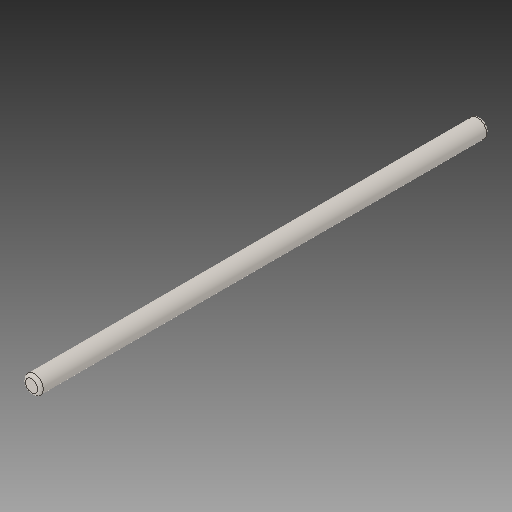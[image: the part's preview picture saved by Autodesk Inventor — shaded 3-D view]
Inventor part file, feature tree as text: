
AUTODESK INVENTOR PART (.ipt)
format: ipt  version: 2018 (Build 220112000, 112)  size: 82,432 bytes
history: native  units: in
note: dims shown in document units (in); Inventor stores cm internally (conversion verified against a paired STEP export)
features: fillet x1
ambient origin geometry x8: Origin, YZ Plane, XZ Plane, XY Plane, X Axis, Y Axis, Z Axis, Center Point
bodies: Solid1 (feature_tree)
feature tree (1):
  fillet  "Fillet1"  [1 undecoded]
note: 1 required parameter value undecoded (feature->parameter linkage not recoverable at this tier; creation-order binding heuristic only, values carry confidence <= 0.55)
